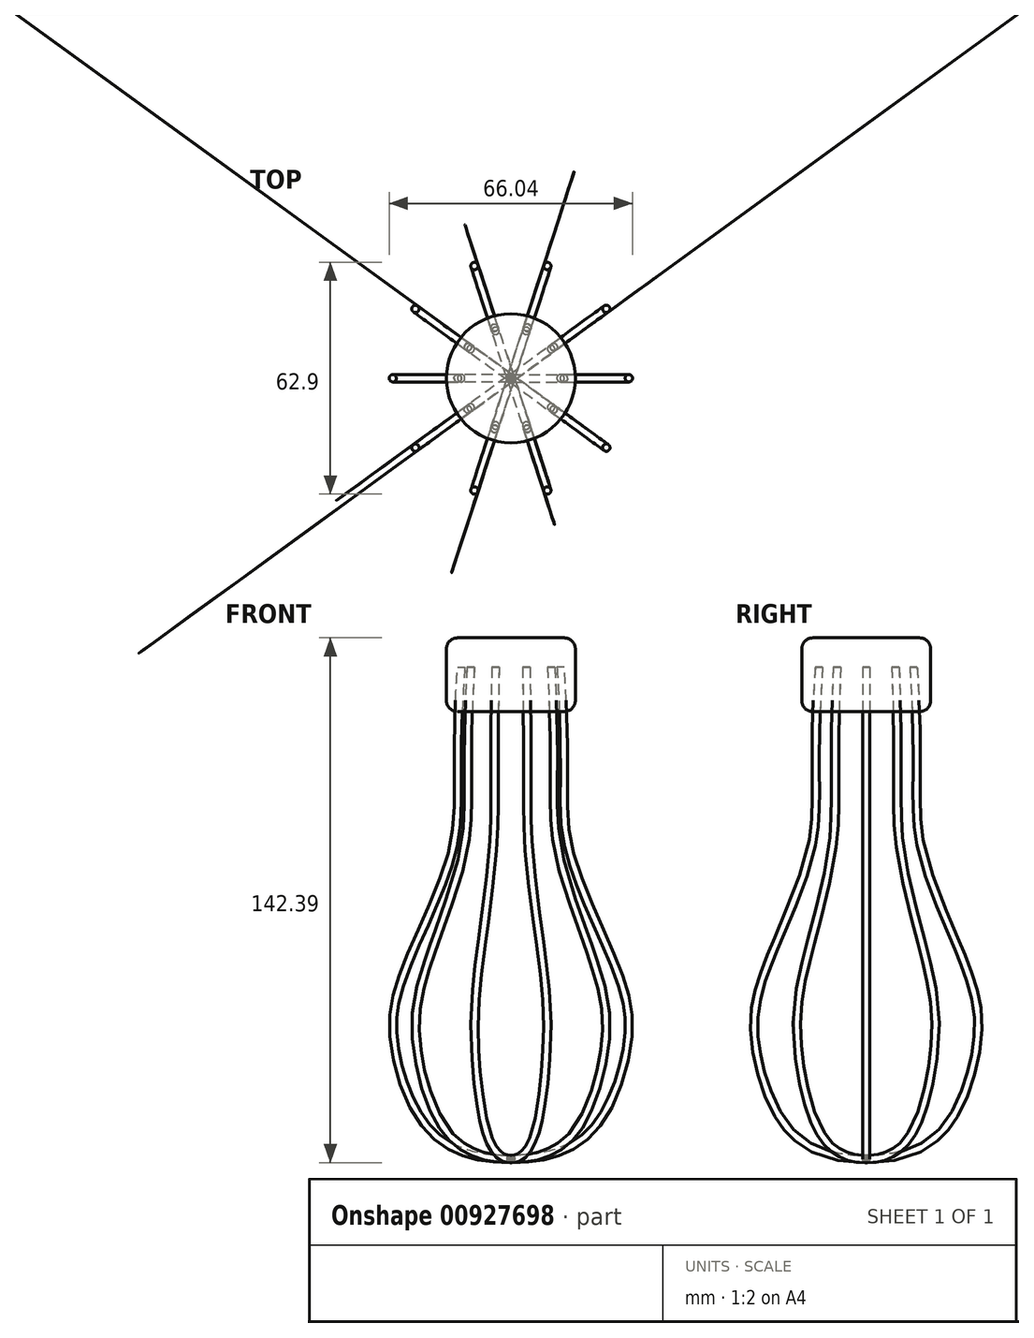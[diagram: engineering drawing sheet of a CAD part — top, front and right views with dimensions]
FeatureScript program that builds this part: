
annotation { "Feature Type Name" : "Feature", "Feature Type Description" : "" }
export const myFeature = defineFeature(function(context is Context, id is Id, definition is map)
    precondition{}
    {
        {
            var Q0;
            Q0=qCreatedBy(makeId("Front.planeOp"),FACE);
            var sketch = newSketch(context, id + "F0", { "sketchPlane" : qUnion([Q0])});
            skFitSpline(sketch, "E0", {"points": [v(18.69, 76.8) * mm, v(20.83, 28.32) * mm, v(32.1, 0) * mm, v(37.15, -22.53) * mm, v(27.56, -50.36) * mm, v(13.33, -60.16) * mm, v(0, -61.89) * mm], "startDerivative": vector(28.21, -404.12) * mm, "endDerivative": vector(-117.03, 0.38) * mm});
            skLineSegment(sketch, "E1", {"start": v(0, 76.72) * mm, "end": v(0, -80.64) * mm, "construction": true});
            skSolve(sketch);
        }
        {
            var Q0;
            Q0=qCreatedBy(makeId("Top.planeOp"),FACE);
            cPlane(context, id + "F1", {"entities" : qUnion([Q0]), "cplaneType" : CPlaneType.OFFSET, "offset" : 74.68 * mm, "width" : 152.4 * mm, "height" : 152.4 * mm});
        }
        {
            var Q0;
            Q0=qCreatedBy(id+"F1.planeOp",FACE);
            var sketch = newSketch(context, id + "F2", { "sketchPlane" : qUnion([Q0])});
            skCircle(sketch, "E2", {"center": v(13.64, 0) * mm, "radius": 1 * mm});
            skSolve(sketch);
        }
        {
            var Q0;
            Q0=makeQuery(id+"F2.imprint","IMPRINT",FACE,{"disambiguationData":[TD([[makeQuery(id+"F2.imprint","IMPRINT",EDGE,{"derivedFrom":sQuery(id+"F2.wireOp",EDGE,"E2")}),1.0]])]});
            var Q1;
            Q1=sQuery(id+"F0.wireOp",EDGE,"E0");
            sweep(context, id + "F3", {"profiles" : qUnion([Q0]), "path" : qUnion([Q1])});
        }
        {
            var Q0;
            Q0=qCreatedBy(makeId("Front.planeOp"),FACE);
            var sketch = newSketch(context, id + "F4", { "sketchPlane" : qUnion([Q0])});
            skLineSegment(sketch, "E3", {"start": v(0, 73.88) * mm, "end": v(0, -65.6) * mm, "construction": true});
            skSolve(sketch);
        }
        {
            var Q0;
            Q0=makeQuery(id+"F3.opSweep","SWEPT_BODY",BODY,{"disambiguationData":[OSD([sQuery(id+"F0.wireOp",EDGE,"E0"),sQuery(id+"F2.wireOp",EDGE,"E2")])]});
            var Q1;
            Q1=sQuery(id+"F4.wireOp",EDGE,"E3");
            circularPattern(context, id + "F5", {"entities" : qUnion([Q0]), "axis" : qUnion([Q1]), "angle" : 360 * degree, "instanceCount" : 10, "equalSpace" : true});
        }
        {
            var Q0;
            Q0=qCreatedBy(id+"F1.planeOp",FACE);
            var sketch = newSketch(context, id + "F6", { "sketchPlane" : qUnion([Q0])});
            skCircle(sketch, "E4", {"center": v(0, 0) * mm, "radius": 17.5 * mm});
            skSolve(sketch);
        }
        {
            var Q0;
            Q0=makeQuery(id+"F6.imprint","IMPRINT",FACE,{"disambiguationData":[TD([[makeQuery(id+"F6.imprint","IMPRINT",EDGE,{"derivedFrom":sQuery(id+"F6.wireOp",EDGE,"E4")}),1.0]])]});
            extrude(context, id + "F7", {"entities" : qUnion([Q0]), "endBound" : BoundingType.SYMMETRIC, "depth" : 20 * mm, "offsetDistance" : 25 * mm});
        }
        {
            var Q0;
            Q0=makeQuery(id+"F7.opExtrude","CAP_EDGE",EDGE,{"disambiguationData":[OSD([sQuery(id+"F6.wireOp",EDGE,"E4")])],"isStart":true});
            var Q1;
            Q1=makeQuery(id+"F7.opExtrude","CAP_EDGE",EDGE,{"disambiguationData":[OSD([sQuery(id+"F6.wireOp",EDGE,"E4")])],"isStart":false});
            fillet(context, id + "F8", {"entities" : qUnion([Q0, Q1]), "radius" : 3 * mm, "tangentPropagation" : true, "allowEdgeOverflow" : false});
        }
    });
